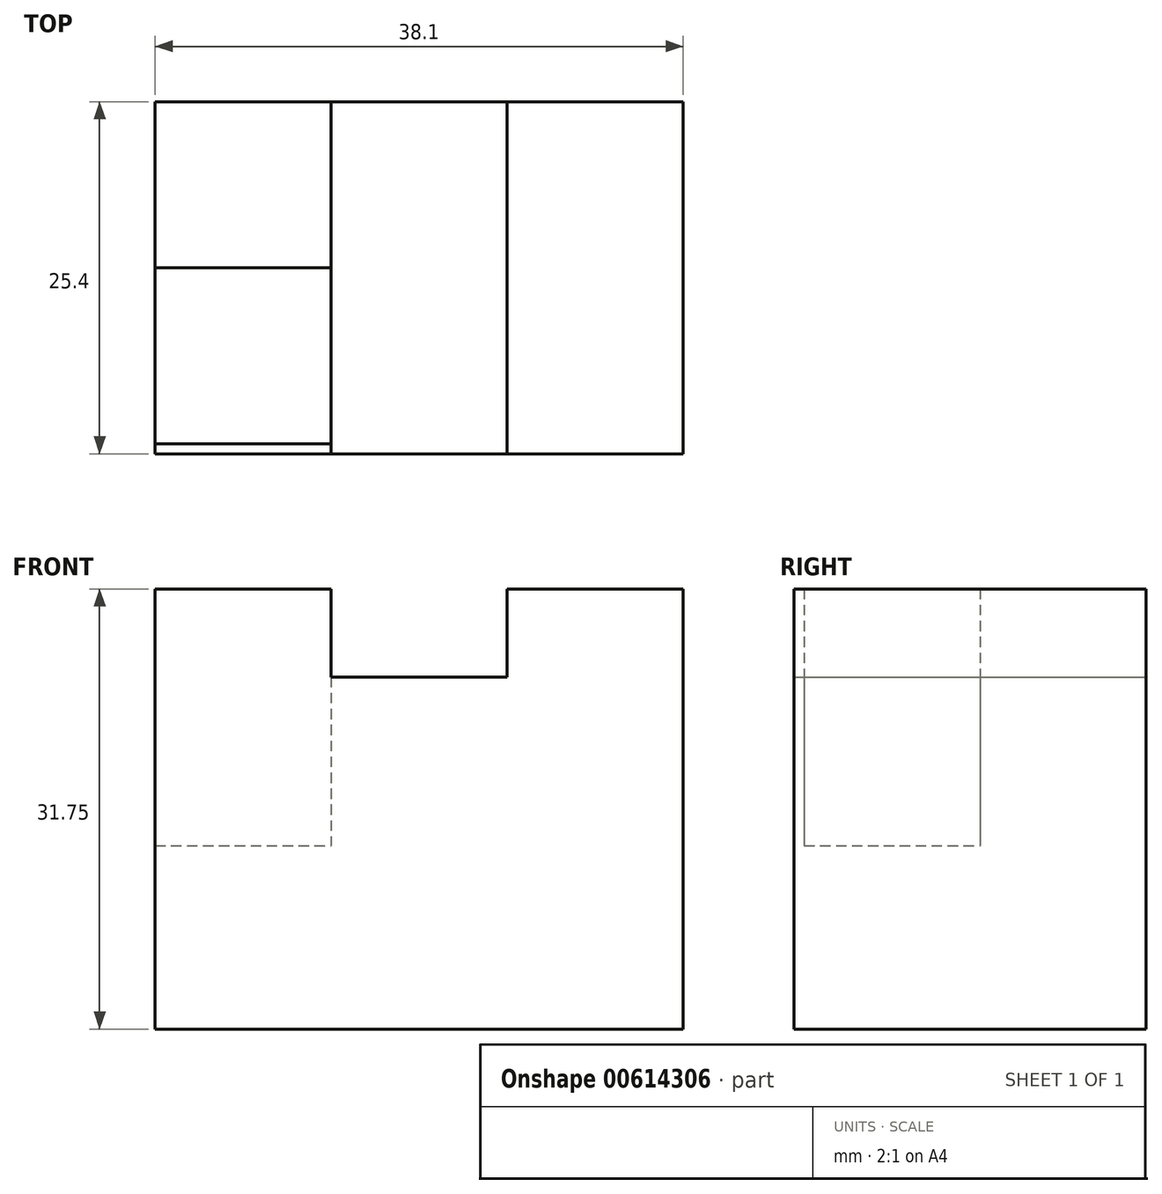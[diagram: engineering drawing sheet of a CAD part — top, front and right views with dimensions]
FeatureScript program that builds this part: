
annotation { "Feature Type Name" : "Feature", "Feature Type Description" : "" }
export const myFeature = defineFeature(function(context is Context, id is Id, definition is map)
    precondition{}
    {
        {
            var Q0;
            Q0=qCreatedBy(makeId("Front.planeOp"),FACE);
            var sketch = newSketch(context, id + "F0", { "sketchPlane" : qUnion([Q0])});
            skLineSegment(sketch, "E0.bottom", {"start": v(-12.7, -6.28) * mm, "end": v(25.4, -6.28) * mm});
            skLineSegment(sketch, "E0.top", {"start": v(-12.7, -18.98) * mm, "end": v(25.4, -18.98) * mm});
            skLineSegment(sketch, "E0.left", {"start": v(-12.7, -6.28) * mm, "end": v(-12.7, -18.98) * mm});
            skLineSegment(sketch, "E0.right", {"start": v(25.4, -6.28) * mm, "end": v(25.4, -18.98) * mm});
            skLineSegment(sketch, "E1", {"start": v(-12.7, -6.28) * mm, "end": v(-12.7, 12.77) * mm});
            skLineSegment(sketch, "E2", {"start": v(-12.7, 12.77) * mm, "end": v(0, 12.77) * mm});
            skLineSegment(sketch, "E3", {"start": v(0, 12.77) * mm, "end": v(0, 6.42) * mm});
            skLineSegment(sketch, "E4", {"start": v(0, 6.42) * mm, "end": v(12.7, 6.42) * mm});
            skLineSegment(sketch, "E5", {"start": v(12.7, 6.42) * mm, "end": v(12.7, 12.77) * mm});
            skLineSegment(sketch, "E6", {"start": v(12.7, 12.77) * mm, "end": v(25.4, 12.77) * mm});
            skLineSegment(sketch, "E7", {"start": v(25.4, 12.77) * mm, "end": v(25.4, -6.28) * mm});
            skSolve(sketch);
        }
        {
            var Q0;
            Q0 = qSketchRegion(id + "F0", true);
            extrude(context, id + "F1", {"entities" : qUnion([Q0]), "depth" : 25.4 * mm, "offsetDistance" : 25.4 * mm});
        }
        {
            var Q0;
            Q0=qCreatedBy(makeId("Right.planeOp"),FACE);
            var sketch = newSketch(context, id + "F2", { "sketchPlane" : qUnion([Q0])});
            skLineSegment(sketch, "E8.bottom", {"start": v(-24.67, 13.3) * mm, "end": v(-11.97, 13.3) * mm});
            skLineSegment(sketch, "E8.top", {"start": v(-24.67, -5.74) * mm, "end": v(-11.97, -5.74) * mm});
            skLineSegment(sketch, "E8.left", {"start": v(-24.67, 13.3) * mm, "end": v(-24.67, -5.74) * mm});
            skLineSegment(sketch, "E8.right", {"start": v(-11.97, 13.3) * mm, "end": v(-11.97, -5.74) * mm});
            skSolve(sketch);
        }
        {
            var Q0;
            Q0=makeQuery(id+"F2.imprint","IMPRINT",FACE,{"disambiguationData":[TD([[makeQuery(id+"F2.imprint","IMPRINT",EDGE,{"derivedFrom":sQuery(id+"F2.wireOp",EDGE,"E8.bottom")}),-1.0]])]});
            extrude(context, id + "F3", {"entities" : qUnion([Q0]), "operationType" : NewBodyOperationType.REMOVE, "oppositeDirection" : true, "depth" : 25.4 * mm, "offsetDistance" : 25.4 * mm});
        }
    });
